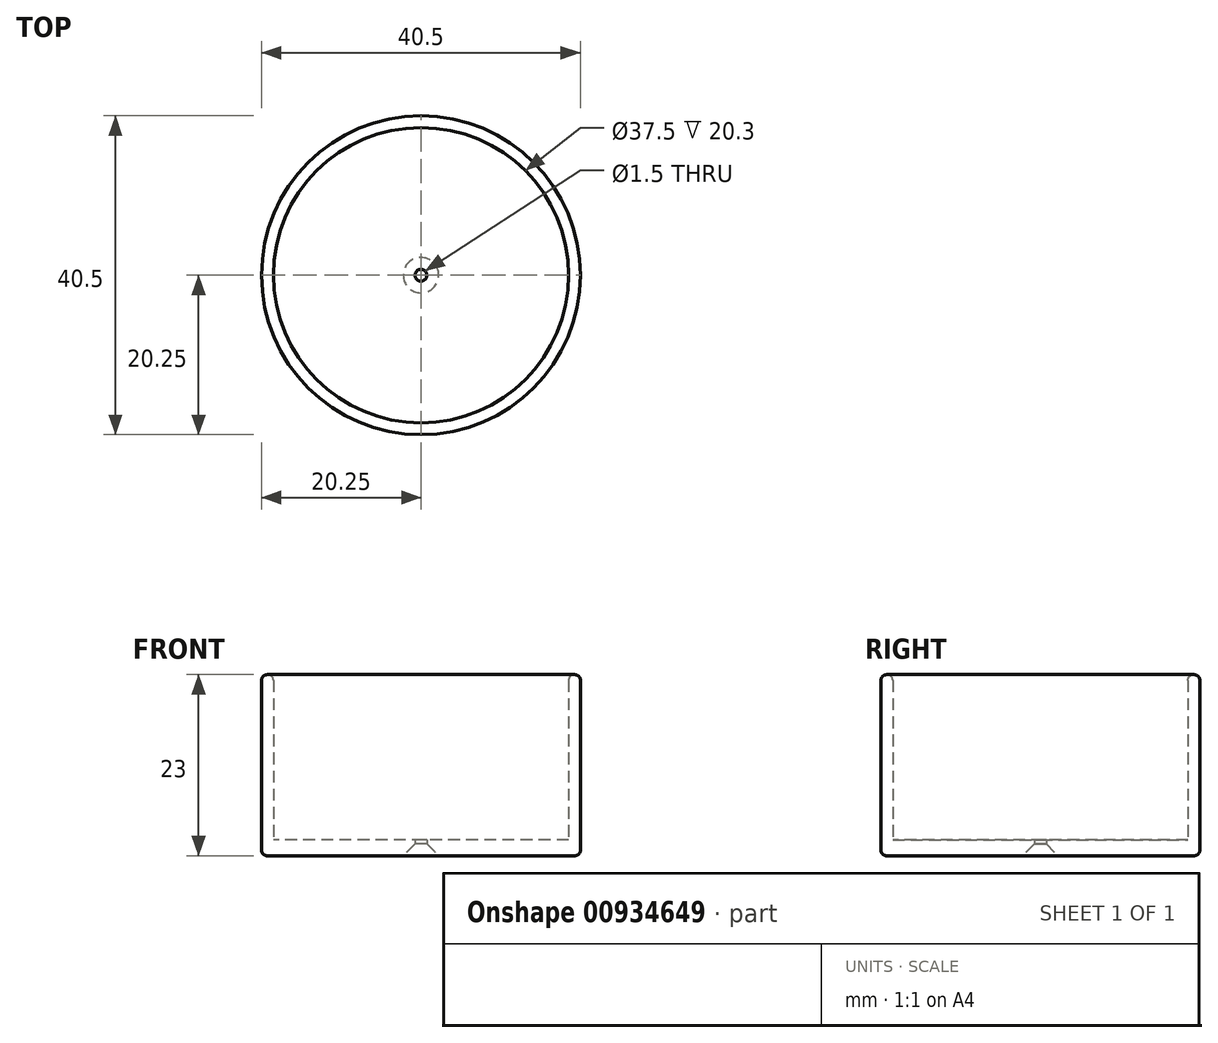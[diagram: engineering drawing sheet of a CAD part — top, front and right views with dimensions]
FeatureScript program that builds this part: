
annotation { "Feature Type Name" : "Feature", "Feature Type Description" : "" }
export const myFeature = defineFeature(function(context is Context, id is Id, definition is map)
    precondition{}
    {
        {
            var Q0;
            Q0=qCreatedBy(makeId("Top.planeOp"),FACE);
            var sketch = newSketch(context, id + "F0", { "sketchPlane" : qUnion([Q0])});
            skCircle(sketch, "E0", {"center": v(0, 0) * mm, "radius": 18.75 * mm});
            skCircle(sketch, "E1.0", {"center": v(0, 0) * mm, "radius": 20.25 * mm});
            skCircle(sketch, "E2", {"center": v(0, 0) * mm, "radius": 0.75 * mm});
            skSolve(sketch);
        }
        {
            var Q0;
            Q0=makeQuery(id+"F0.imprint","IMPRINT",FACE,{"disambiguationData":[TD([[makeQuery(id+"F0.imprint","IMPRINT",EDGE,{"derivedFrom":sQuery(id+"F0.wireOp",EDGE,"E0")}),-1.0]])]});
            extrude(context, id + "F1", {"entities" : qUnion([Q0]), "depth" : 23 * mm, "offsetDistance" : 25 * mm});
        }
        {
            var Q0;
            Q0=makeQuery(id+"F0.imprint","IMPRINT",FACE,{"disambiguationData":[TD([[makeQuery(id+"F0.imprint","IMPRINT",EDGE,{"derivedFrom":sQuery(id+"F0.wireOp",EDGE,"E0")}),1.0]])]});
            extrude(context, id + "F2", {"entities" : qUnion([Q0]), "operationType" : NewBodyOperationType.ADD, "depth" : 2 * mm, "offsetDistance" : 25 * mm});
        }
        {
            var Q0;
            Q0=makeQuery(id+"F1.opExtrude","CAP_EDGE",EDGE,{"disambiguationData":[OSD([sQuery(id+"F0.wireOp",EDGE,"E1.0")])],"isStart":false});
            var Q1;
            Q1=makeQuery(id+"F1.opExtrude","CAP_EDGE",EDGE,{"disambiguationData":[OSD([sQuery(id+"F0.wireOp",EDGE,"E0")])],"isStart":false});
            var Q2;
            Q2=makeQuery(id+"F1.opExtrude","CAP_EDGE",EDGE,{"disambiguationData":[OSD([sQuery(id+"F0.wireOp",EDGE,"E1.0")])],"isStart":true});
            fillet(context, id + "F3", {"entities" : qUnion([Q0, Q1, Q2]), "radius" : 0.7 * mm, "tangentPropagation" : true, "allowEdgeOverflow" : false});
        }
        {
            var Q0;
            Q0=makeQuery(id+"F2.opExtrude","CAP_EDGE",EDGE,{"disambiguationData":[OSD([sQuery(id+"F0.wireOp",EDGE,"E2")])],"isStart":true});
            chamfer(context, id + "F4", {"entities" : qUnion([Q0]), "chamferType" : ChamferType.OFFSET_ANGLE, "width" : 1.5 * mm, "oppositeDirection" : false, "angle" : 45 * degree, "tangentPropagation" : true});
        }
    });
